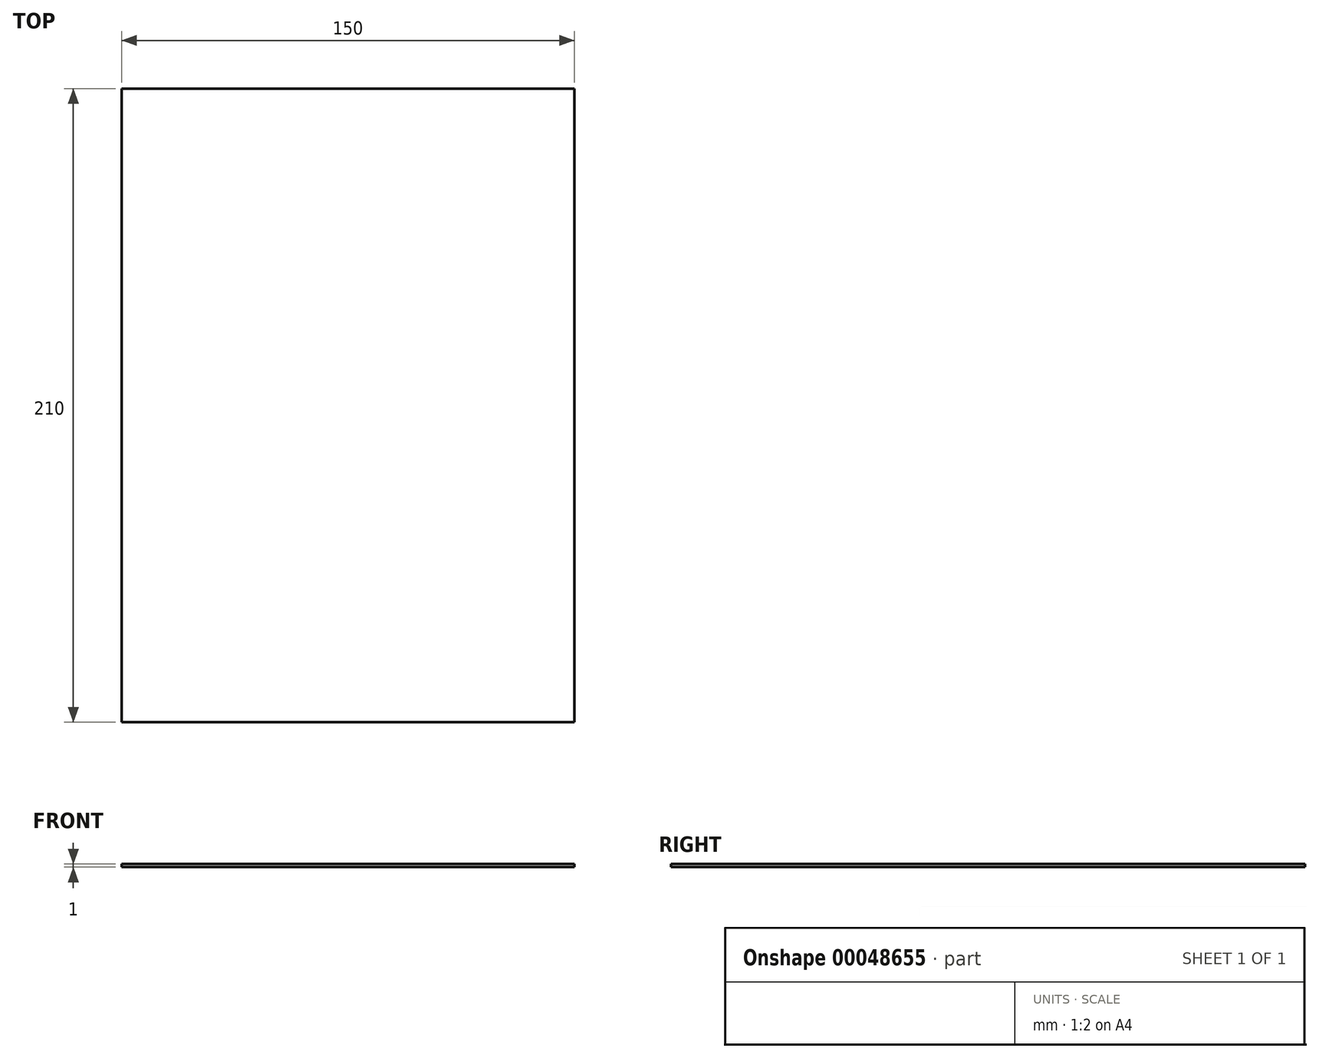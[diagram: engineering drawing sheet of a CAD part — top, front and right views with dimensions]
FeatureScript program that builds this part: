
annotation { "Feature Type Name" : "Feature", "Feature Type Description" : "" }
export const myFeature = defineFeature(function(context is Context, id is Id, definition is map)
    precondition{}
    {
        {
            var Q0;
            Q0=qCreatedBy(makeId("Top.planeOp"),FACE);
            var sketch = newSketch(context, id + "F0", { "sketchPlane" : qUnion([Q0])});
            skLineSegment(sketch, "E0.bottom", {"start": v(-76.03, 111.68) * mm, "end": v(73.97, 111.68) * mm});
            skLineSegment(sketch, "E0.top", {"start": v(-76.03, -98.32) * mm, "end": v(73.97, -98.32) * mm});
            skLineSegment(sketch, "E0.left", {"start": v(-76.03, 111.68) * mm, "end": v(-76.03, -98.32) * mm});
            skLineSegment(sketch, "E0.right", {"start": v(73.97, 111.68) * mm, "end": v(73.97, -98.32) * mm});
            skSolve(sketch);
        }
        {
            var Q0;
            Q0=makeQuery(id+"F0.imprint","IMPRINT",FACE,{"disambiguationData":[TD([[makeQuery(id+"F0.imprint","IMPRINT",EDGE,{"derivedFrom":sQuery(id+"F0.wireOp",EDGE,"E0.bottom")}),-1.0]])]});
            extrude(context, id + "F1", {"entities" : qUnion([Q0]), "depth" : 1 * mm});
        }
    });
